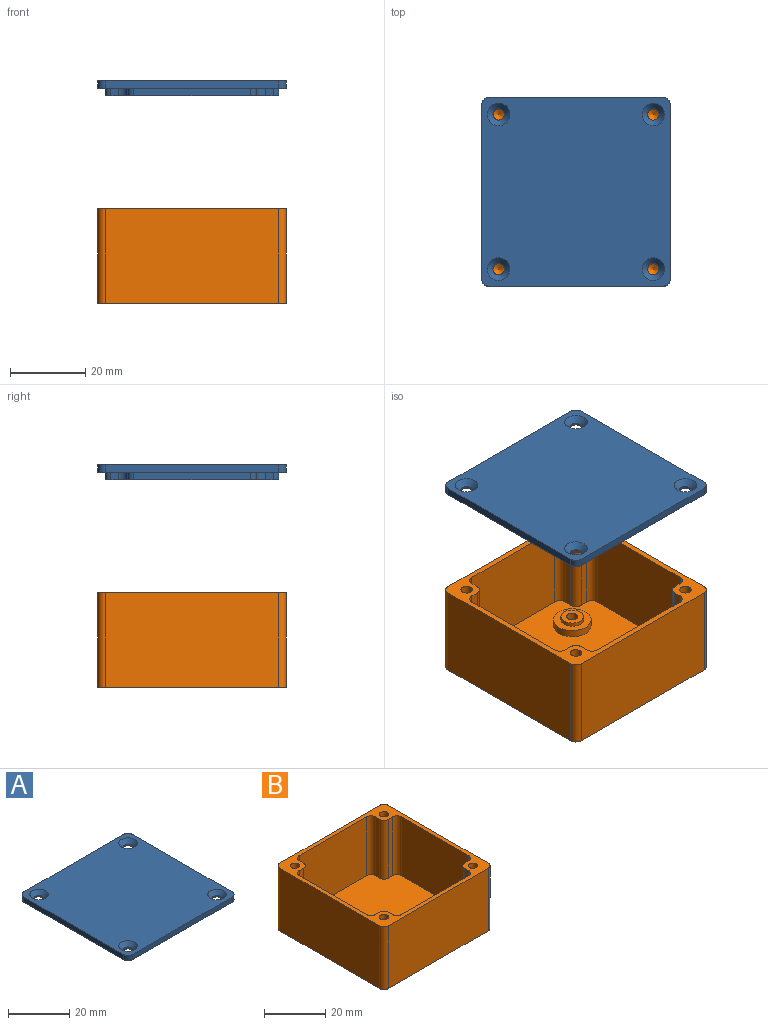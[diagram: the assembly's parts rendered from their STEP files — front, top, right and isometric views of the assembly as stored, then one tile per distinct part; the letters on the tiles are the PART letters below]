
ASSEMBLY  parts=2 mates=1
PART A: 43 faces, bbox 50x50x4 mm
  f0: plane 46x2mm, normal (0,1,0), area 92mm2, adj f4,f5,f8,f33
  f1: plane 46x2mm, normal (-1,0,0), area 92mm2, adj f4,f6,f8,f33
  f2: plane 46x2mm, normal (0,-1,0), area 92mm2, adj f6,f7,f8,f33
  f3: plane 46x2mm, normal (1,0,0), area 92mm2, adj f5,f7,f8,f33
  f4: cylinder r=2mm len=2mm, axis (0,0,1), area 6.3mm2, adj f0,f1,f8,f33
  f5: cylinder r=2mm len=2mm, axis (0,0,-1), area 6.3mm2, adj f0,f3,f8,f33
  f6: cylinder r=2mm len=2mm, axis (0,0,-1), area 6.3mm2, adj f1,f2,f8,f33
  f7: cylinder r=2mm len=2mm, axis (0,0,1), area 6.3mm2, adj f2,f3,f8,f33
  f8: plane 50x50mm, normal (0,0,1), area 2383.5mm2, adj f0,f1,f2,f3,f4,f5,f6,f7
  f9: cylinder r=1.5mm len=2mm, axis (0,0,-1), area 4.7mm2, adj f10,f32,f33,f34
  f10: plane 2x2mm, normal (0,1,0), area 4mm2, adj f9,f11,f33,f34
  f11: cylinder r=2.5mm len=2.5mm, axis (0,0,-1), area 7.9mm2, adj f10,f12,f33,f34
  f12: plane 2x2mm, normal (-1,0,0), area 4mm2, adj f11,f13,f33,f34
  f13: cylinder r=1.5mm len=2mm, axis (0,0,-1), area 4.7mm2, adj f12,f14,f33,f34
  f14: plane 31x2mm, normal (0,1,0), area 62mm2, adj f13,f15,f33,f34
  f15: cylinder r=1.5mm len=2mm, axis (0,0,-1), area 4.7mm2, adj f14,f16,f33,f34
  f16: plane 2x2mm, normal (1,0,0), area 4mm2, adj f15,f17,f33,f34
  f17: cylinder r=2.5mm len=2.5mm, axis (0,0,-1), area 7.9mm2, adj f16,f18,f33,f34
  f18: plane 2x2mm, normal (0,1,0), area 4mm2, adj f17,f19,f33,f34
  f19: cylinder r=1.5mm len=2mm, axis (0,0,-1), area 4.7mm2, adj f18,f20,f33,f34
  f20: plane 31x2mm, normal (1,0,0), area 62mm2, adj f19,f21,f33,f34
  f21: cylinder r=1.5mm len=2mm, axis (0,0,-1), area 4.7mm2, adj f20,f22,f33,f34
  f22: plane 2x2mm, normal (0,-1,0), area 4mm2, adj f21,f23,f33,f34
  f23: cylinder r=2.5mm len=2.5mm, axis (0,0,-1), area 7.9mm2, adj f22,f24,f33,f34
  f24: plane 2x2mm, normal (1,0,0), area 4mm2, adj f23,f25,f33,f34
  f25: cylinder r=1.5mm len=2mm, axis (0,0,-1), area 4.7mm2, adj f24,f26,f33,f34
  f26: plane 31x2mm, normal (0,-1,0), area 62mm2, adj f25,f27,f33,f34
  f27: cylinder r=1.5mm len=2mm, axis (0,0,-1), area 4.7mm2, adj f26,f28,f33,f34
  f28: plane 2x2mm, normal (-1,0,0), area 4mm2, adj f27,f29,f33,f34
  f29: cylinder r=2.5mm len=2.5mm, axis (0,0,-1), area 7.9mm2, adj f28,f30,f33,f34
  f30: plane 2x2mm, normal (0,-1,0), area 4mm2, adj f29,f31,f33,f34
  f31: cylinder r=1.5mm len=2mm, axis (0,0,-1), area 4.7mm2, adj f30,f32,f33,f34
  f32: plane 31x2mm, normal (-1,0,0), area 62mm2, adj f9,f31,f33,f34
  f33: plane 50x50mm, normal (0,0,-1), area 494.8mm2, adj f0,f1,f2,f3,f4,f5,f6,f7
  f34: plane 46x46mm, normal (0,0,-1), area 1973.5mm2, adj f9,f10,f11,f12,f13,f14,f15,f16
  f35: cylinder r=1.5mm len=3mm, axis (0,0,-1), area 4.7mm2, adj f33,f41
  f36: cylinder r=1.5mm len=3mm, axis (0,0,-1), area 4.7mm2, adj f33,f42
  f37: cylinder r=1.5mm len=3mm, axis (0,0,-1), area 4.7mm2, adj f33,f39
  f38: cylinder r=1.5mm len=3mm, axis (0,0,-1), area 4.7mm2, adj f33,f40
  f39: cone r=3mm half-angle=45deg, axis (0,0,1), area 30mm2, adj f8,f37
  f40: cone r=3mm half-angle=45deg, axis (0,0,1), area 30mm2, adj f8,f38
  f41: cone r=3mm half-angle=45deg, axis (0,0,1), area 30mm2, adj f8,f35
  f42: cone r=3mm half-angle=45deg, axis (0,0,1), area 30mm2, adj f8,f36
PART B: 67 faces, bbox 50x50x25 mm
  f0: cylinder r=1.5mm len=3mm, axis (0,0,-1), area 23.6mm2, adj f46,f66
  f1: cylinder r=1.5mm len=3mm, axis (0,0,-1), area 23.6mm2, adj f48,f59
  f2: plane 47x47mm, normal (0,0,1), area 1904.5mm2, adj f3,f4,f5,f6,f13,f14,f15,f16
  f3: plane 31x23.5mm, normal (0,1,0), area 728.5mm2, adj f2,f7,f37,f39
  f4: plane 31x23.5mm, normal (-1,0,0), area 728.5mm2, adj f2,f7,f32,f35
  f5: plane 31x23.5mm, normal (1,0,0), area 728.5mm2, adj f2,f7,f29,f38
  f6: plane 31x23.5mm, normal (0,-1,0), area 728.5mm2, adj f2,f7,f31,f33
  f7: plane 50x50mm, normal (0,0,1), area 406.7mm2, adj f3,f4,f5,f6,f8,f9,f10,f11
  f8: plane 46x25mm, normal (0,-1,0), area 1150mm2, adj f7,f12,f41,f44
  f9: plane 46x25mm, normal (1,0,0), area 1150mm2, adj f7,f12,f41,f42
  f10: plane 46x25mm, normal (0,1,0), area 1150mm2, adj f7,f12,f42,f43
  f11: plane 46x25mm, normal (-1,0,0), area 1150mm2, adj f7,f12,f43,f44
  f12: plane 50x50mm, normal (0,0,-1), area 2449.8mm2, adj f8,f9,f10,f11,f41,f42,f43,f44
  f13: plane 23.5x2mm, normal (0,-1,0), area 47mm2, adj f2,f7,f29,f30
  f14: plane 23.5x2mm, normal (1,0,0), area 47mm2, adj f2,f7,f30,f31
  f15: plane 23.5x2mm, normal (0,-1,0), area 47mm2, adj f2,f7,f32,f34
  f16: plane 23.5x2mm, normal (-1,0,0), area 47mm2, adj f2,f7,f33,f34
  f17: plane 23.5x2mm, normal (0,1,0), area 47mm2, adj f2,f7,f38,f40
  f18: plane 23.5x2mm, normal (1,0,0), area 47mm2, adj f2,f7,f39,f40
  f19: plane 23.5x2mm, normal (0,1,0), area 47mm2, adj f2,f7,f35,f36
  f20: plane 23.5x2mm, normal (-1,0,0), area 47mm2, adj f2,f7,f36,f37
  f21: cone r=0mm half-angle=59deg, axis (0,0,1), area 8.2mm2, adj f22
  f22: cylinder r=1.5mm len=20mm, axis (0,0,1), area 188.5mm2, adj f7,f21
  f23: cone r=0mm half-angle=59deg, axis (0,0,1), area 8.2mm2, adj f24
  f24: cylinder r=1.5mm len=20mm, axis (0,0,1), area 188.5mm2, adj f7,f23
  f25: cone r=0mm half-angle=59deg, axis (0,0,1), area 8.2mm2, adj f26
  f26: cylinder r=1.5mm len=20mm, axis (0,0,1), area 188.5mm2, adj f7,f25
  f27: cone r=0mm half-angle=59deg, axis (0,0,1), area 8.2mm2, adj f28
  f28: cylinder r=1.5mm len=20mm, axis (0,0,1), area 188.5mm2, adj f7,f27
  f29: cylinder r=2mm len=23.5mm, axis (0,0,-1), area 73.8mm2, adj f2,f5,f7,f13
  f30: cylinder r=2mm len=23.5mm, axis (0,0,1), area 73.8mm2, adj f2,f7,f13,f14
  f31: cylinder r=2mm len=23.5mm, axis (0,0,-1), area 73.8mm2, adj f2,f6,f7,f14
  f32: cylinder r=2mm len=23.5mm, axis (0,0,-1), area 73.8mm2, adj f2,f4,f7,f15
  f33: cylinder r=2mm len=23.5mm, axis (0,0,1), area 73.8mm2, adj f2,f6,f7,f16
  f34: cylinder r=2mm len=23.5mm, axis (0,0,1), area 73.8mm2, adj f2,f7,f15,f16
  f35: cylinder r=2mm len=23.5mm, axis (0,0,1), area 73.8mm2, adj f2,f4,f7,f19
  f36: cylinder r=2mm len=23.5mm, axis (0,0,1), area 73.8mm2, adj f2,f7,f19,f20
  f37: cylinder r=2mm len=23.5mm, axis (0,0,1), area 73.8mm2, adj f2,f3,f7,f20
  f38: cylinder r=2mm len=23.5mm, axis (0,0,1), area 73.8mm2, adj f2,f5,f7,f17
  f39: cylinder r=2mm len=23.5mm, axis (0,0,-1), area 73.8mm2, adj f2,f3,f7,f18
  f40: cylinder r=2mm len=23.5mm, axis (0,0,1), area 73.8mm2, adj f2,f7,f17,f18
  f41: cylinder r=2mm len=25mm, axis (0,0,-1), area 78.5mm2, adj f7,f8,f9,f12
  f42: cylinder r=2mm len=25mm, axis (0,0,1), area 78.5mm2, adj f7,f9,f10,f12
  f43: cylinder r=2mm len=25mm, axis (0,0,-1), area 78.5mm2, adj f7,f10,f11,f12
  f44: cylinder r=2mm len=25mm, axis (0,0,1), area 78.5mm2, adj f7,f8,f11,f12
  f45: cylinder r=3mm len=6mm, axis (0,0,-1), area 18.8mm2, adj f46,f50
  f46: plane 6x6mm, normal (0,0,1), area 21.2mm2, adj f0,f45
  f47: cylinder r=3mm len=6mm, axis (0,0,-1), area 18.8mm2, adj f48,f52
  f48: plane 6x6mm, normal (0,0,1), area 21.2mm2, adj f1,f47
  f49: cylinder r=5mm len=10mm, axis (0,0,-1), area 62.8mm2, adj f2,f50
  f50: plane 10x10mm, normal (0,0,1), area 50.3mm2, adj f45,f49
  f51: cylinder r=5mm len=10mm, axis (0,0,-1), area 62.8mm2, adj f2,f52
  f52: plane 10x10mm, normal (0,0,1), area 50.3mm2, adj f47,f51
  f53: plane 3x2mm, normal (0,-1,0), area 6mm2, adj f12,f54,f58,f59
  f54: plane 2.6x2mm, normal (-0.87,-0.5,0), area 6mm2, adj f12,f53,f55,f59
  f55: plane 2.6x2mm, normal (-0.87,0.5,0), area 6mm2, adj f12,f54,f56,f59
  f56: plane 3x2mm, normal (0,1,0), area 6mm2, adj f12,f55,f57,f59
  f57: plane 2.6x2mm, normal (0.87,0.5,0), area 6mm2, adj f12,f56,f58,f59
  f58: plane 2.6x2mm, normal (0.87,-0.5,0), area 6mm2, adj f12,f53,f57,f59
  f59: plane 6x5.2mm, normal (0,0,-1), area 16.3mm2, adj f1,f53,f54,f55,f56,f57,f58
  f60: plane 3x2mm, normal (0,-1,0), area 6mm2, adj f12,f61,f65,f66
  f61: plane 2.6x2mm, normal (-0.87,-0.5,0), area 6mm2, adj f12,f60,f62,f66
  f62: plane 2.6x2mm, normal (-0.87,0.5,0), area 6mm2, adj f12,f61,f63,f66
  f63: plane 3x2mm, normal (0,1,0), area 6mm2, adj f12,f62,f64,f66
  f64: plane 2.6x2mm, normal (0.87,0.5,0), area 6mm2, adj f12,f63,f65,f66
  f65: plane 2.6x2mm, normal (0.87,-0.5,0), area 6mm2, adj f12,f60,f64,f66
  f66: plane 6x5.2mm, normal (0,0,-1), area 16.3mm2, adj f0,f60,f61,f62,f63,f64,f65
PLACE A t=(-16.89,27.06,14.41)mm
PLACE B rot(axis=(0,0,-1),180deg) t=(83.11,27.06,7.48)mm
MATE slider B.f27 <-> A.f35  axis (0,0,1) through (62.61,47.56,7.48)mm
